# Revit family: 3459A.1_NX_Wall_Mount_Occupancy_Sensors
name_source: partatom
category: Communication Devices
revit_build: Autodesk Revit 2014 (Build: 20130308_1515(x64)
units: mm (PartAtom-declared; Revit-internal decimal feet)

## types (1)
- 3459A.1_NX_Wall_Mount_Occupancy_Sensors
    Assembly Code = D5090
    Certifications = UL and cUL listed
    Default Elevation = 48 "
    Description = key component in a NX Network Lighting Control System, providing programmable switching and dimming control of the projects lighting circuits
    Feartures = • IntelliDAPT self-adaptive technology – no manual adjustment required
• Occupancy or vacancy operation selectable per load when used with the
NX Room Controller
• All-digital sensor
• Non-volatile memory for sensor settings
• 500 to 2,500 square-foot coverage area (based on model)
• Plug and play integration with NX Room Controller
• UL and cUL listed
• Low voltage device: 24 VDC
    Housing Material = Paint - Hubbell - Matte White
    Manufacturer = Hubbell Control Solutions
    Model = NX Ceiling Mount Occupancy Sensors employ Passive Infrared
and Ultrasonic sensing technologies to turn lighting on and off based
on occupancy
    Patents = U.S. Patents: 615129, 5946209, 5699243, 5640143, 6078253, D404326, 6222191, 5986357, 6759954
Patent(s) Pending
    Power Requirements = Powered by NX Room Controller using plenum rated CAT5 cables (ordered separately)
    Product Documentation Link = https://hubbellcdn.com
    Product Page URL = https://www.hubbell.com
    Sensing Element = Metal-Hubbell-Nickel
    Type Comments = Wall Mount Occupancy Sensors
    URL = https://www.hubbell.com
    Warranty = 5-Years Warranty

## geometry (parser evidence)
native form markers: Sweep x3
no freeform markers — native parametric forms only
